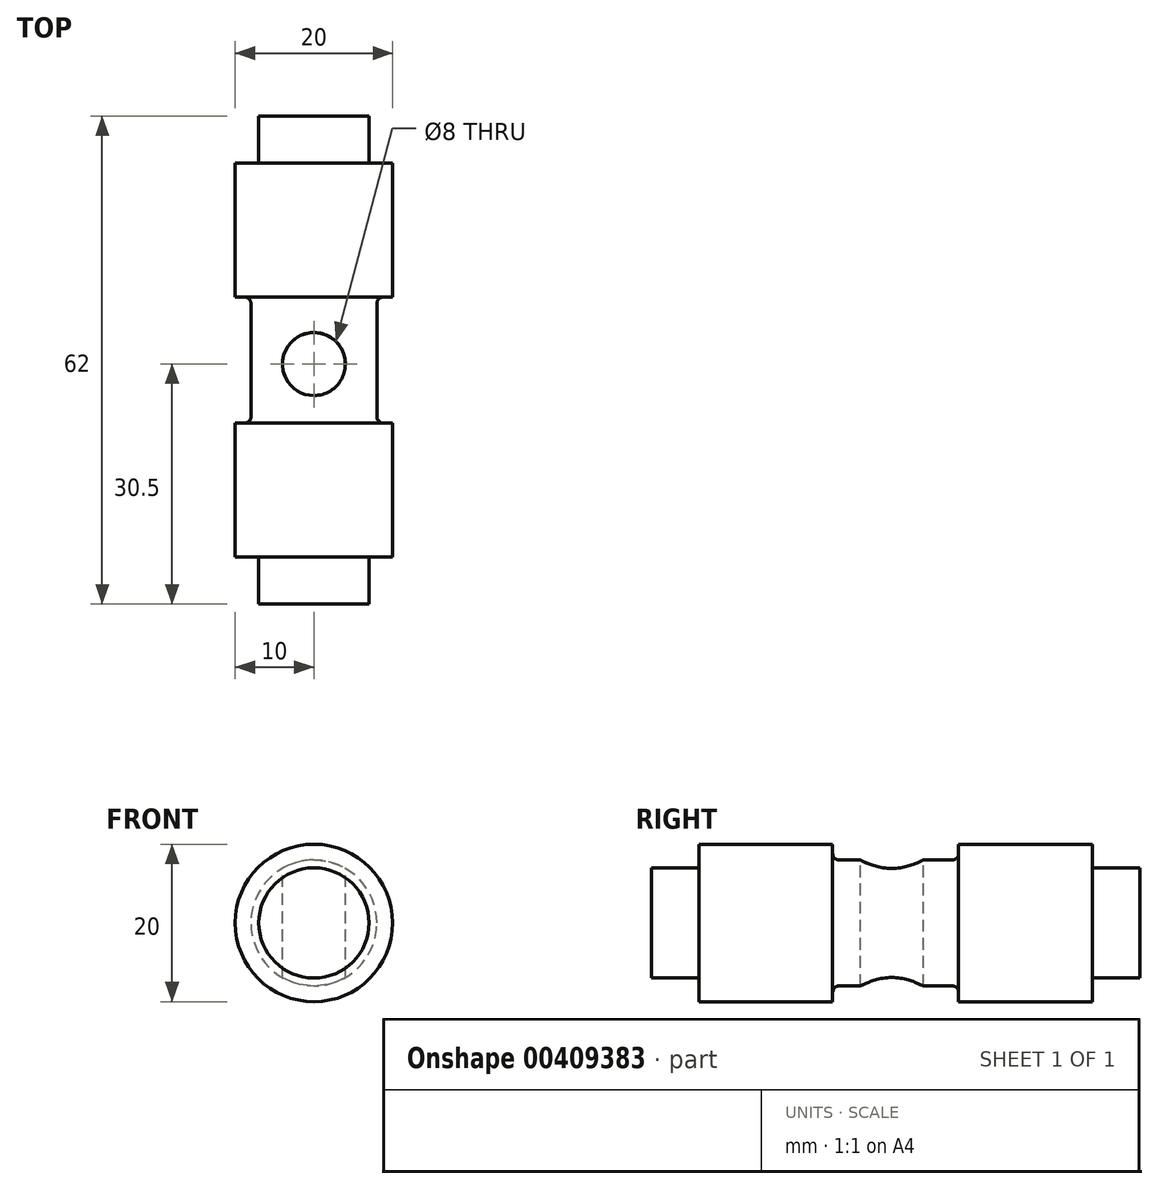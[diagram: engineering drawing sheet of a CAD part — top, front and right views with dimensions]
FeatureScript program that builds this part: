
annotation { "Feature Type Name" : "Feature", "Feature Type Description" : "" }
export const myFeature = defineFeature(function(context is Context, id is Id, definition is map)
    precondition{}
    {
        {
            var Q0;
            Q0=qCreatedBy(makeId("Right.planeOp"),FACE);
            var sketch = newSketch(context, id + "F0", { "sketchPlane" : qUnion([Q0])});
            skLineSegment(sketch, "E0", {"start": v(0, 0) * mm, "end": v(0, 7) * mm});
            skLineSegment(sketch, "E1", {"start": v(0, 7) * mm, "end": v(6, 7) * mm});
            skLineSegment(sketch, "E2", {"start": v(6, 7) * mm, "end": v(6, 10) * mm});
            skLineSegment(sketch, "E3", {"start": v(6, 10) * mm, "end": v(23, 10) * mm});
            skLineSegment(sketch, "E4", {"start": v(23, 10) * mm, "end": v(23, 8.8) * mm});
            skLineSegment(sketch, "E5", {"start": v(23.8, 8) * mm, "end": v(38.2, 8) * mm});
            skLineSegment(sketch, "E6", {"start": v(39, 8.8) * mm, "end": v(39, 10) * mm});
            skLineSegment(sketch, "E7", {"start": v(39, 10) * mm, "end": v(56, 10) * mm});
            skLineSegment(sketch, "E8", {"start": v(56, 10) * mm, "end": v(56, 7) * mm});
            skLineSegment(sketch, "E9", {"start": v(56, 7) * mm, "end": v(62, 7) * mm});
            skLineSegment(sketch, "E10", {"start": v(62, 7) * mm, "end": v(62, 0) * mm});
            skLineSegment(sketch, "E11", {"start": v(62, 0) * mm, "end": v(0, 0) * mm});
            skPoint(sketch, "E12.visualSharp", {"position": v(23, 8) * mm});
            skArc(sketch, "E12.filletArc", {"start": v(23, 8.8) * mm, "mid": v(23.23, 8.23) * mm, "end": v(23.8, 8) * mm});
            skPoint(sketch, "E13.visualSharp", {"position": v(39, 8) * mm});
            skArc(sketch, "E13.filletArc", {"start": v(38.2, 8) * mm, "mid": v(38.77, 8.23) * mm, "end": v(39, 8.8) * mm});
            skSolve(sketch);
        }
        {
            var Q0;
            Q0=makeQuery(id+"F0.imprint","IMPRINT",FACE,{"disambiguationData":[TD([[makeQuery(id+"F0.imprint","IMPRINT",EDGE,{"derivedFrom":sQuery(id+"F0.wireOp",EDGE,"E0")}),-1.0]])]});
            var Q1;
            Q1=sQuery(id+"F0.wireOp",EDGE,"E11");
            revolve(context, id + "F1", {"entities" : qUnion([Q0]), "axis" : qUnion([Q1]), "revolveType" : RevolveType.FULL});
        }
        {
            var Q0;
            Q0=qCreatedBy(makeId("Top.planeOp"),FACE);
            cPlane(context, id + "F2", {"entities" : qUnion([Q0]), "cplaneType" : CPlaneType.OFFSET, "offset" : 8 * mm, "width" : 150 * mm, "height" : 150 * mm});
        }
        {
            var Q0;
            Q0=qCreatedBy(id+"F2.planeOp",FACE);
            var sketch = newSketch(context, id + "F3", { "sketchPlane" : qUnion([Q0])});
            skPoint(sketch, "E14", {"position": v(0, 30.5) * mm});
            skCircle(sketch, "E15", {"center": v(0, 30.5) * mm, "radius": 4 * mm});
            skSolve(sketch);
        }
        {
            var Q0;
            Q0=makeQuery(id+"F3.imprint","IMPRINT",FACE,{"disambiguationData":[TD([[makeQuery(id+"F3.imprint","IMPRINT",EDGE,{"derivedFrom":sQuery(id+"F3.wireOp",EDGE,"E15")}),1.0]])]});
            extrude(context, id + "F4", {"entities" : qUnion([Q0]), "operationType" : NewBodyOperationType.REMOVE, "endBound" : BoundingType.THROUGH_ALL, "oppositeDirection" : true, "depth" : 25 * mm});
        }
    });
